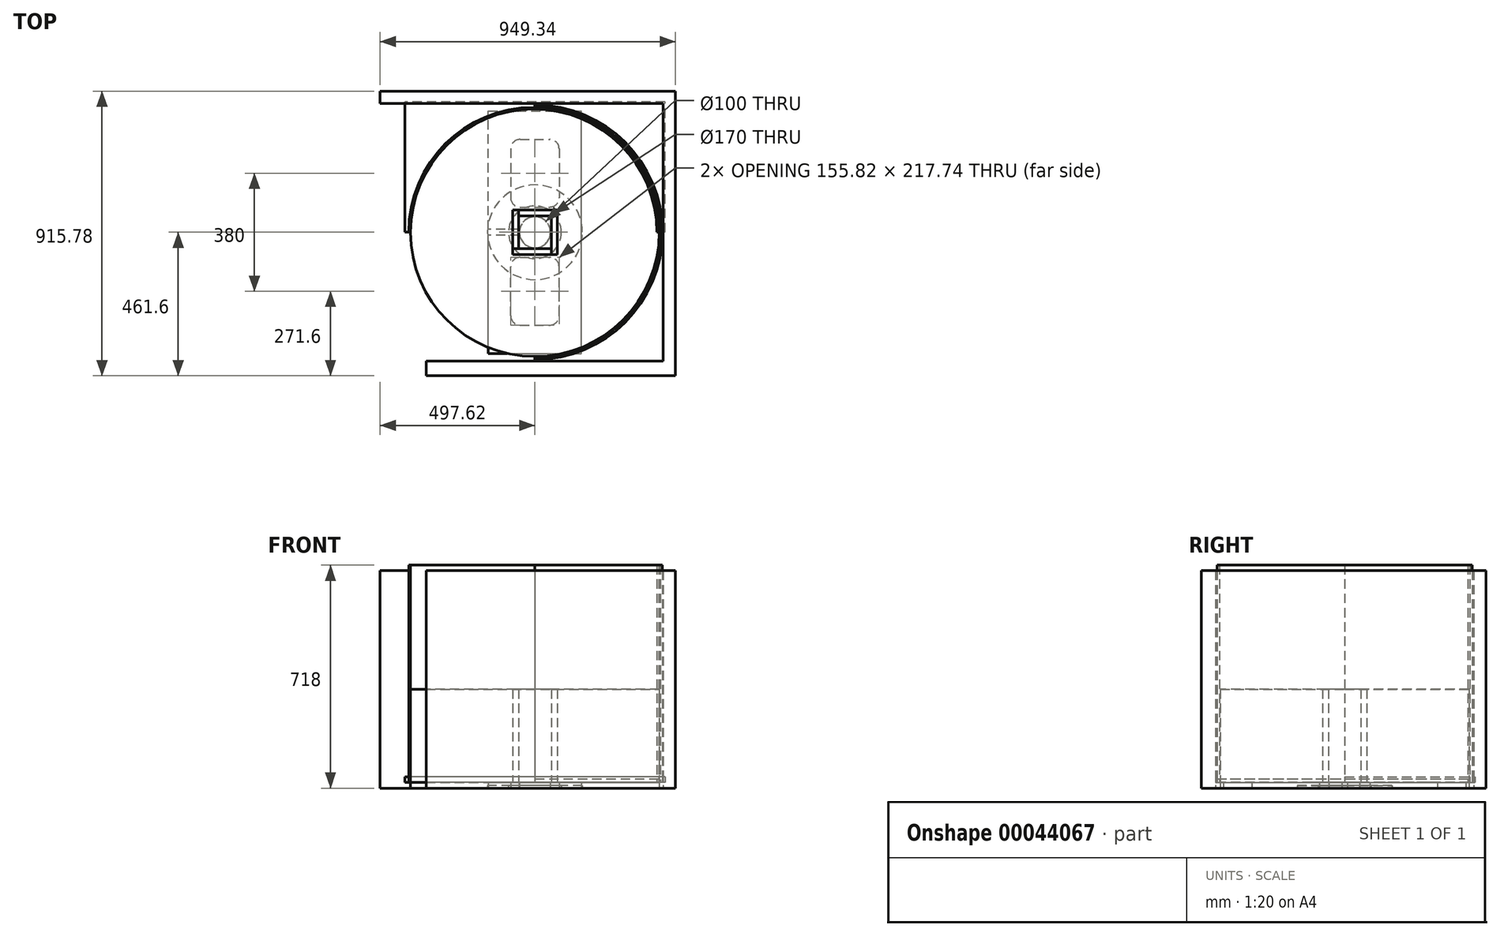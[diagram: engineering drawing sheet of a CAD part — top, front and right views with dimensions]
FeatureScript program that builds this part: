
annotation { "Feature Type Name" : "Feature", "Feature Type Description" : "" }
export const myFeature = defineFeature(function(context is Context, id is Id, definition is map)
    precondition{}
    {
        {
            var Q0;
            Q0=qCreatedBy(makeId("Top.planeOp"),FACE);
            var sketch = newSketch(context, id + "F0", { "sketchPlane" : qUnion([Q0])});
            skCircle(sketch, "E0", {"center": v(0, 0) * mm, "radius": 85 * mm});
            skCircle(sketch, "E1", {"center": v(0, 0) * mm, "radius": 152.5 * mm});
            skSolve(sketch);
        }
        {
            var Q0;
            Q0 = qSketchRegion(id + "F0", true);
            extrude(context, id + "F1", {"entities" : qUnion([Q0]), "depth" : 8 * mm});
        }
        {
            var Q0;
            Q0=qCreatedBy(makeId("Top.planeOp"),FACE);
            var sketch = newSketch(context, id + "F2", { "sketchPlane" : qUnion([Q0])});
            skCircle(sketch, "E2", {"center": v(0, 0) * mm, "radius": 400 * mm});
            skSolve(sketch);
        }
        {
            var Q0;
            Q0 = qSketchRegion(id + "F2", true);
            extrude(context, id + "F3", {"entities" : qUnion([Q0]), "depth" : 18 * mm});
        }
        {
            var Q0;
            Q0=makeQuery(id+"F3.opExtrude","CAP_FACE",FACE,{"disambiguationData":[OSD([sQuery(id+"F2.wireOp",EDGE,"E2")])],"isStart":false});
            var sketch = newSketch(context, id + "F4", { "sketchPlane" : qUnion([Q0])});
            skLineSegment(sketch, "E3.rect.bottom", {"start": v(50, -50) * mm, "end": v(-50, -50) * mm});
            skLineSegment(sketch, "E3.rect.top", {"start": v(50, 50) * mm, "end": v(-50, 50) * mm});
            skLineSegment(sketch, "E3.rect.left", {"start": v(50, -50) * mm, "end": v(50, 50) * mm});
            skLineSegment(sketch, "E3.rect.right", {"start": v(-50, -50) * mm, "end": v(-50, 50) * mm});
            skPoint(sketch, "E3.rect.middle", {"position": v(0, 0) * mm});
            skSolve(sketch);
        }
        {
            var Q0;
            Q0 = qSketchRegion(id + "F4", true);
            extrude(context, id + "F5", {"entities" : qUnion([Q0]), "depth" : 300 * mm});
        }
        {
            var Q0;
            Q0=makeQuery(id+"F5.opExtrude","SWEPT_BODY",BODY,{"disambiguationData":[OSD([sQuery(id+"F4.wireOp",EDGE,"E3.rect.bottom"),sQuery(id+"F4.wireOp",EDGE,"E3.rect.top"),sQuery(id+"F4.wireOp",EDGE,"E3.rect.left"),sQuery(id+"F4.wireOp",EDGE,"E3.rect.right")])]});
            deleteBodies(context, id + "F6", {"entities" : qUnion([Q0])});
        }
        {
            var Q0;
            Q0=makeQuery(id+"F3.opExtrude","CAP_FACE",FACE,{"disambiguationData":[OSD([sQuery(id+"F2.wireOp",EDGE,"E2")])],"isStart":false});
            var sketch = newSketch(context, id + "F7", { "sketchPlane" : qUnion([Q0])});
            skLineSegment(sketch, "E4", {"start": v(0, 0) * mm, "end": v(400, 0) * mm});
            skLineSegment(sketch, "E5", {"start": v(0, 0) * mm, "end": v(0, 400) * mm});
            skLineSegment(sketch, "E6", {"start": v(0, 0) * mm, "end": v(0, -400) * mm, "construction": true});
            skLineSegment(sketch, "E7", {"start": v(0, 0) * mm, "end": v(-400, 0) * mm, "construction": true});
            skLineSegment(sketch, "E8.0", {"start": v(-9, 9) * mm, "end": v(-358.14, 9) * mm});
            skLineSegment(sketch, "E8.1", {"start": v(-9, 9) * mm, "end": v(-9, 358.14) * mm});
            skLineSegment(sketch, "E9.0", {"start": v(9, 9) * mm, "end": v(358.14, 9) * mm});
            skLineSegment(sketch, "E9.1", {"start": v(9, 9) * mm, "end": v(9, 358.14) * mm});
            skLineSegment(sketch, "E10.0", {"start": v(-9, -9) * mm, "end": v(-9, -358.14) * mm});
            skLineSegment(sketch, "E10.1", {"start": v(-9, -9) * mm, "end": v(-358.14, -9) * mm});
            skLineSegment(sketch, "E11.0", {"start": v(9, -9) * mm, "end": v(9, -358.14) * mm});
            skLineSegment(sketch, "E11.1", {"start": v(9, -9) * mm, "end": v(358.14, -9) * mm});
            skSolve(sketch);
        }
        {
            var Q0;
            {var subQ16=sQuery(id+"F7.wireOp",EDGE,"E4");Q0=makeQuery(id+"F7.imprint","IMPRINT",FACE,{"disambiguationData":[TD([[makeQuery(id+"F7.imprint","IMPRINT",EDGE,{"derivedFrom":subQ16}),-1.0]])]});}
            var Q1;
            {var subQ6=sQuery(id+"F7.wireOp",EDGE,"E4");Q1=makeQuery(id+"F7.imprint","IMPRINT",FACE,{"disambiguationData":[TD([[makeQuery(id+"F7.imprint","IMPRINT",EDGE,{"derivedFrom":subQ6}),1.0]])]});}
            var Q2;
            Q2=sQuery(id+"F7.wireOp",EDGE,"E10.1");
            var Q3;
            Q3=sQuery(id+"F7.wireOp",EDGE,"E8.0");
            extrude(context, id + "F8", {"entities" : qUnion([Q0, Q1]), "surfaceEntities" : qUnion([Q2, Q3]), "depth" : 300 * mm});
        }
        {
            var Q0;
            Q0=qCreatedBy(makeId("Top.planeOp"),FACE);
            var sketch = newSketch(context, id + "F9", { "sketchPlane" : qUnion([Q0])});
            skLineSegment(sketch, "E12", {"start": v(0, 415) * mm, "end": v(411.72, 415) * mm});
            skLineSegment(sketch, "E13", {"start": v(411.72, 0) * mm, "end": v(411.72, 415) * mm});
            skLineSegment(sketch, "E14.MirrorCS", {"start": v(0, -415) * mm, "end": v(411.72, -415) * mm});
            skLineSegment(sketch, "E15.MirrorCS", {"start": v(411.72, 0) * mm, "end": v(411.72, -415) * mm});
            skLineSegment(sketch, "E16", {"start": v(0, 415) * mm, "end": v(-497.62, 415) * mm});
            skLineSegment(sketch, "E17", {"start": v(0, -415) * mm, "end": v(-350, -415) * mm});
            skLineSegment(sketch, "E18", {"start": v(-497.62, 415) * mm, "end": v(-497.62, 454.18) * mm});
            skLineSegment(sketch, "E19", {"start": v(-497.62, 454.18) * mm, "end": v(451.72, 454.18) * mm});
            skLineSegment(sketch, "E20", {"start": v(451.72, 454.18) * mm, "end": v(451.72, -461.6) * mm});
            skLineSegment(sketch, "E21", {"start": v(451.72, -461.6) * mm, "end": v(-350, -461.6) * mm});
            skLineSegment(sketch, "E22", {"start": v(-350, -461.6) * mm, "end": v(-350, -415) * mm});
            skSolve(sketch);
        }
        {
            var Q0;
            Q0 = qSketchRegion(id + "F9", true);
            extrude(context, id + "F10", {"entities" : qUnion([Q0]), "depth" : 700 * mm});
        }
        {
            var Q0;
            Q0=qCreatedBy(makeId("Top.planeOp"),FACE);
            var sketch = newSketch(context, id + "F11", { "sketchPlane" : qUnion([Q0])});
            skLineSegment(sketch, "E23.rect.bottom", {"start": v(-150, -390) * mm, "end": v(150, -390) * mm});
            skLineSegment(sketch, "E23.rect.top", {"start": v(-150, 390) * mm, "end": v(150, 390) * mm});
            skLineSegment(sketch, "E23.rect.left", {"start": v(-150, -390) * mm, "end": v(-150, -9) * mm});
            skLineSegment(sketch, "E23.rect.right", {"start": v(150, -390) * mm, "end": v(150, 390) * mm});
            skPoint(sketch, "E23.rect.middle", {"position": v(0, 0) * mm});
            skLineSegment(sketch, "E24", {"start": v(0, 0) * mm, "end": v(150, 0) * mm, "construction": true});
            skLineSegment(sketch, "E25", {"start": v(0, 390) * mm, "end": v(0, -390) * mm, "construction": true});
            skLineSegment(sketch, "E26", {"start": v(0, 9) * mm, "end": v(-150, 9) * mm});
            skLineSegment(sketch, "E27", {"start": v(0, 9) * mm, "end": v(0, 0) * mm});
            skLineSegment(sketch, "E28.MirrorCS", {"start": v(0, -9) * mm, "end": v(-150, -9) * mm});
            skLineSegment(sketch, "E29.MirrorCS", {"start": v(0, -9) * mm, "end": v(0, 0) * mm});
            skLineSegment(sketch, "E30.trimOffspring", {"start": v(-150, 9) * mm, "end": v(-150, 390) * mm});
            skPoint(sketch, "E31.orphan", {"position": v(-150, 0) * mm});
            skLineSegment(sketch, "E32.rect.bottom", {"start": v(-47.9, -298.87) * mm, "end": v(47.9, -298.87) * mm});
            skLineSegment(sketch, "E32.rect.top", {"start": v(-47.9, -81.13) * mm, "end": v(47.9, -81.13) * mm});
            skLineSegment(sketch, "E32.rect.left", {"start": v(-77.9, -268.87) * mm, "end": v(-77.9, -111.13) * mm});
            skLineSegment(sketch, "E32.rect.right", {"start": v(77.9, -268.87) * mm, "end": v(77.9, -111.13) * mm});
            skPoint(sketch, "E32.rect.middle", {"position": v(0, -190) * mm});
            skPoint(sketch, "E33.visualSharp", {"position": v(77.9, -81.13) * mm});
            skArc(sketch, "E33.filletArc", {"start": v(77.9, -111.13) * mm, "mid": v(69.12, -89.91) * mm, "end": v(47.9, -81.13) * mm});
            skPoint(sketch, "E34.visualSharp", {"position": v(77.9, -298.87) * mm});
            skArc(sketch, "E34.filletArc", {"start": v(47.9, -298.87) * mm, "mid": v(69.12, -290.09) * mm, "end": v(77.9, -268.87) * mm});
            skPoint(sketch, "E35.visualSharp", {"position": v(-77.9, -298.87) * mm});
            skArc(sketch, "E35.filletArc", {"start": v(-77.9, -268.87) * mm, "mid": v(-69.12, -290.09) * mm, "end": v(-47.9, -298.87) * mm});
            skPoint(sketch, "E36.visualSharp", {"position": v(-77.9, -81.13) * mm});
            skArc(sketch, "E36.filletArc", {"start": v(-47.9, -81.13) * mm, "mid": v(-69.12, -89.91) * mm, "end": v(-77.9, -111.13) * mm});
            skLineSegment(sketch, "E37.MirrorCS", {"start": v(-47.9, 81.13) * mm, "end": v(47.9, 81.13) * mm});
            skArc(sketch, "E38.MirrorCS", {"start": v(77.9, 111.13) * mm, "mid": v(69.12, 89.91) * mm, "end": v(47.9, 81.13) * mm});
            skLineSegment(sketch, "E39.MirrorCS", {"start": v(77.9, 268.87) * mm, "end": v(77.9, 111.13) * mm});
            skArc(sketch, "E40.MirrorCS", {"start": v(47.9, 298.87) * mm, "mid": v(69.12, 290.09) * mm, "end": v(77.9, 268.87) * mm});
            skLineSegment(sketch, "E41.MirrorCS", {"start": v(-47.9, 298.87) * mm, "end": v(47.9, 298.87) * mm});
            skLineSegment(sketch, "E42.MirrorCS", {"start": v(-77.9, 268.87) * mm, "end": v(-77.9, 111.13) * mm});
            skArc(sketch, "E43.MirrorCS", {"start": v(-77.9, 268.87) * mm, "mid": v(-69.12, 290.09) * mm, "end": v(-47.9, 298.87) * mm});
            skPoint(sketch, "E44.MirrorP", {"position": v(-77.9, 81.13) * mm});
            skPoint(sketch, "E45.MirrorP", {"position": v(-77.9, 298.87) * mm});
            skLineSegment(sketch, "E46", {"start": v(-77.9, 111.13) * mm, "end": v(-77.9, 111.13) * mm});
            skLineSegment(sketch, "E47", {"start": v(-47.9, 81.13) * mm, "end": v(-47.9, 81.13) * mm});
            skArc(sketch, "E48.filletArc", {"start": v(-77.9, 111.13) * mm, "mid": v(-69.12, 89.91) * mm, "end": v(-47.9, 81.13) * mm});
            skSolve(sketch);
        }
        {
            var Q0;
            Q0 = qSketchRegion(id + "F11", true);
            extrude(context, id + "F12", {"entities" : qUnion([Q0]), "depth" : 18 * mm});
        }
        {
            var Q0;
            Q0=makeQuery(id+"F3.opExtrude","CAP_FACE",FACE,{"disambiguationData":[OSD([sQuery(id+"F2.wireOp",EDGE,"E2")])],"isStart":false});
            var sketch = newSketch(context, id + "F13", { "sketchPlane" : qUnion([Q0])});
            skCircle(sketch, "E49.0", {"center": v(0, 0) * mm, "radius": 391 * mm});
            skSolve(sketch);
        }
        {
            var Q0;
            Q0=makeQuery(id+"F13.imprint","IMPRINT",FACE,{"disambiguationData":[TD([[makeQuery(id+"F13.imprint","IMPRINT",EDGE,{"derivedFrom":sQuery(id+"F13.wireOp",EDGE,"E49.0")}),1.0]])]});
            var sketch = newSketch(context, id + "F14", { "sketchPlane" : qUnion([Q0])});
            skLineSegment(sketch, "E50.rect.top", {"start": v(418.3, 419.4) * mm, "end": v(-418.3, 419.4) * mm});
            skLineSegment(sketch, "E50.rect.left", {"start": v(418.3, 0) * mm, "end": v(418.3, 419.4) * mm});
            skLineSegment(sketch, "E50.rect.right", {"start": v(-418.3, 0) * mm, "end": v(-418.3, 419.4) * mm});
            skPoint(sketch, "E50.rect.middle", {"position": v(0, 0) * mm});
            skLineSegment(sketch, "E51", {"start": v(-400, 0) * mm, "end": v(-418.3, 0) * mm});
            skLineSegment(sketch, "E52", {"start": v(400, 0) * mm, "end": v(418.3, 0) * mm});
            skPoint(sketch, "E50.rect.bottom.end.orphan", {"position": v(-418.3, -419.4) * mm});
            skPoint(sketch, "E53.orphan", {"position": v(418.3, -419.4) * mm});
            skArc(sketch, "E54.0", {"start": v(398.61, 0) * mm, "mid": v(-3.7, 402.3) * mm, "end": v(-406, 0) * mm});
            skArc(sketch, "E55.0", {"start": v(392.61, 0) * mm, "mid": v(-3.7, 396.3) * mm, "end": v(-400, 0) * mm});
            skLineSegment(sketch, "E56", {"start": v(400, 0) * mm, "end": v(398.61, 0) * mm});
            skLineSegment(sketch, "E57", {"start": v(398.61, 0) * mm, "end": v(392.61, 0) * mm});
            skSolve(sketch);
        }
        {
            var Q0;
            Q0=makeQuery(id+"F14.imprint","IMPRINT",FACE,{"disambiguationData":[TD([[makeQuery(id+"F14.imprint","IMPRINT",EDGE,{"derivedFrom":sQuery(id+"F14.wireOp",EDGE,"E50.rect.top")}),1.0]])]});
            extrude(context, id + "F15", {"entities" : qUnion([Q0]), "depth" : 18 * mm});
        }
        {
            var Q0;
            {var subQ1=sQuery(id+"F14.wireOp",EDGE,"E54.0");Q0=makeQuery(id+"F14.imprint","IMPRINT",FACE,{"disambiguationData":[TD([[makeQuery(id+"F14.imprint","IMPRINT",EDGE,{"derivedFrom":subQ1}),1.0]])]});}
            extrude(context, id + "F16", {"entities" : qUnion([Q0]), "depth" : 700 * mm});
        }
        {
            var Q0;
            Q0=makeQuery(id+"F14.imprint","IMPRINT",FACE,{"disambiguationData":[TD([[makeQuery(id+"F14.imprint","IMPRINT",EDGE,{"derivedFrom":makeQuery(id+"F13.imprint","IMPRINT",EDGE,{"derivedFrom":sQuery(id+"F13.wireOp",EDGE,"E49.0")})}),1.0]])]});
            var sketch = newSketch(context, id + "F17", { "sketchPlane" : qUnion([Q0])});
            skCircle(sketch, "E58", {"center": v(0, 0) * mm, "radius": 50 * mm});
            skLineSegment(sketch, "E59.bottom", {"start": v(52.5, 52.5) * mm, "end": v(-52.5, 52.5) * mm});
            skLineSegment(sketch, "E59.top", {"start": v(52.5, -52.5) * mm, "end": v(-52.5, -52.5) * mm});
            skLineSegment(sketch, "E59.left", {"start": v(52.5, 52.5) * mm, "end": v(52.5, -52.5) * mm});
            skLineSegment(sketch, "E59.right", {"start": v(-52.5, 52.5) * mm, "end": v(-52.5, -52.5) * mm});
            skLineSegment(sketch, "E60.0", {"start": v(71.5, 71.5) * mm, "end": v(-71.5, 71.5) * mm});
            skLineSegment(sketch, "E60.1", {"start": v(71.5, 71.5) * mm, "end": v(71.5, -71.5) * mm});
            skLineSegment(sketch, "E60.2", {"start": v(71.5, -71.5) * mm, "end": v(-71.5, -71.5) * mm});
            skLineSegment(sketch, "E60.3", {"start": v(-71.5, 71.5) * mm, "end": v(-71.5, -71.5) * mm});
            skLineSegment(sketch, "E61", {"start": v(52.5, -52.5) * mm, "end": v(52.5, -71.5) * mm});
            skLineSegment(sketch, "E62", {"start": v(-52.5, -52.5) * mm, "end": v(-71.5, -52.5) * mm});
            skLineSegment(sketch, "E63", {"start": v(-52.5, 52.5) * mm, "end": v(-52.5, 71.5) * mm});
            skLineSegment(sketch, "E64", {"start": v(52.5, 52.5) * mm, "end": v(71.5, 52.5) * mm});
            skCircle(sketch, "E65.0", {"center": v(0, 0) * mm, "radius": 400 * mm});
            skSolve(sketch);
        }
        {
            var Q0;
            Q0=makeQuery(id+"F17.imprint","IMPRINT",FACE,{"disambiguationData":[TD([[makeQuery(id+"F17.imprint","IMPRINT",EDGE,{"derivedFrom":sQuery(id+"F17.wireOp",EDGE,"E58")}),1.0]])]});
            extrude(context, id + "F18", {"entities" : qUnion([Q0]), "operationType" : NewBodyOperationType.REMOVE, "oppositeDirection" : true, "depth" : 25 * mm, "offsetDistance" : 25 * mm});
        }
        {
            var Q0;
            Q0=makeQuery(id+"F17.imprint","IMPRINT",FACE,{"disambiguationData":[TD([[makeQuery(id+"F17.imprint","IMPRINT",EDGE,{"derivedFrom":sQuery(id+"F17.wireOp",EDGE,"E59.bottom")}),-1.0]])]});
            var Q1;
            Q1=makeQuery(id+"F17.imprint","IMPRINT",FACE,{"disambiguationData":[TD([[makeQuery(id+"F17.imprint","IMPRINT",EDGE,{"derivedFrom":sQuery(id+"F17.wireOp",EDGE,"E59.top")}),1.0]])]});
            extrude(context, id + "F19", {"entities" : qUnion([Q0, Q1]), "depth" : 300 * mm, "offsetDistance" : 25 * mm});
        }
        {
            var Q0;
            Q0=makeQuery(id+"F17.imprint","IMPRINT",FACE,{"disambiguationData":[TD([[makeQuery(id+"F17.imprint","IMPRINT",EDGE,{"derivedFrom":sQuery(id+"F17.wireOp",EDGE,"E59.right")}),-1.0]])]});
            var Q1;
            Q1=makeQuery(id+"F17.imprint","IMPRINT",FACE,{"disambiguationData":[TD([[makeQuery(id+"F17.imprint","IMPRINT",EDGE,{"derivedFrom":sQuery(id+"F17.wireOp",EDGE,"E59.left")}),1.0]])]});
            extrude(context, id + "F20", {"entities" : qUnion([Q0, Q1]), "depth" : 300 * mm, "offsetDistance" : 25 * mm});
        }
        {
            var Q0;
            Q0=makeQuery(id+"F3.opExtrude","CAP_FACE",FACE,{"disambiguationData":[OSD([sQuery(id+"F2.wireOp",EDGE,"E2")])],"isStart":false});
            var sketch = newSketch(context, id + "F21", { "sketchPlane" : qUnion([Q0])});
            skLineSegment(sketch, "E66.0", {"start": v(411.72, 415) * mm, "end": v(0, 415) * mm});
            skLineSegment(sketch, "E66.1", {"start": v(411.72, -415) * mm, "end": v(411.72, 415) * mm});
            skLineSegment(sketch, "E66.2", {"start": v(0, -415) * mm, "end": v(411.72, -415) * mm});
            skLineSegment(sketch, "E67", {"start": v(0, -415) * mm, "end": v(0, -403) * mm});
            skArc(sketch, "E68.0", {"start": v(0, -410) * mm, "mid": v(410, 0) * mm, "end": v(0, 410) * mm});
            skArc(sketch, "E69.0", {"start": v(0, -403) * mm, "mid": v(403, 0) * mm, "end": v(0, 403) * mm});
            skPoint(sketch, "E70.orphan", {"position": v(-497.62, 415) * mm});
            skPoint(sketch, "E71.orphan", {"position": v(-350, -415) * mm});
            skLineSegment(sketch, "E72.trimOffspring", {"start": v(0, 403) * mm, "end": v(0, 415) * mm});
            skSolve(sketch);
        }
        {
            var Q0;
            {var subQ3=sQuery(id+"F21.wireOp",EDGE,"E66.0");Q0=makeQuery(id+"F21.imprint","IMPRINT",FACE,{"disambiguationData":[TD([[makeQuery(id+"F21.imprint","IMPRINT",EDGE,{"derivedFrom":subQ3}),1.0]])]});}
            extrude(context, id + "F22", {"entities" : qUnion([Q0]), "depth" : 12 * mm, "offsetDistance" : 25 * mm});
        }
        {
            var Q0;
            {var subQ2=sQuery(id+"F21.wireOp",EDGE,"E68.0");Q0=makeQuery(id+"F21.imprint","IMPRINT",FACE,{"disambiguationData":[TD([[makeQuery(id+"F21.imprint","IMPRINT",EDGE,{"derivedFrom":subQ2}),1.0]])]});}
            extrude(context, id + "F23", {"entities" : qUnion([Q0]), "depth" : 700 * mm, "offsetDistance" : 25 * mm});
        }
        {
            var Q0;
            Q0=makeQuery(id+"F17.imprint","IMPRINT",FACE,{"disambiguationData":[TD([[makeQuery(id+"F17.imprint","IMPRINT",EDGE,{"derivedFrom":sQuery(id+"F17.wireOp",EDGE,"E58")}),1.0]])]});
            extrude(context, id + "F24", {"entities" : qUnion([Q0]), "operationType" : NewBodyOperationType.REMOVE, "endBound" : BoundingType.THROUGH_ALL, "oppositeDirection" : true, "depth" : 25 * mm, "offsetDistance" : 25 * mm});
        }
        {
            var Q0;
            Q0=makeQuery(id+"F17.imprint","IMPRINT",FACE,{"disambiguationData":[TD([[makeQuery(id+"F17.imprint","IMPRINT",EDGE,{"derivedFrom":sQuery(id+"F17.wireOp",EDGE,"E59.right")}),-1.0]])]});
            var Q1;
            Q1=makeQuery(id+"F17.imprint","IMPRINT",FACE,{"disambiguationData":[TD([[makeQuery(id+"F17.imprint","IMPRINT",EDGE,{"derivedFrom":sQuery(id+"F17.wireOp",EDGE,"E59.left")}),1.0]])]});
            extrude(context, id + "F25", {"entities" : qUnion([Q0, Q1]), "depth" : 300 * mm, "offsetDistance" : 25 * mm});
        }
        {
            var Q0;
            Q0=makeQuery(id+"F17.imprint","IMPRINT",FACE,{"disambiguationData":[TD([[makeQuery(id+"F17.imprint","IMPRINT",EDGE,{"derivedFrom":sQuery(id+"F17.wireOp",EDGE,"E59.bottom")}),-1.0]])]});
            var Q1;
            Q1=makeQuery(id+"F17.imprint","IMPRINT",FACE,{"disambiguationData":[TD([[makeQuery(id+"F17.imprint","IMPRINT",EDGE,{"derivedFrom":sQuery(id+"F17.wireOp",EDGE,"E59.top")}),1.0]])]});
            extrude(context, id + "F26", {"entities" : qUnion([Q0, Q1]), "depth" : 300 * mm, "offsetDistance" : 25 * mm});
        }
    });
